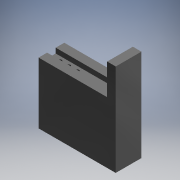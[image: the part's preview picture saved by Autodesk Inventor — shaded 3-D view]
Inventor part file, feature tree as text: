
AUTODESK INVENTOR PART (.ipt)
format: ipt  version: 2019 (Build 230136000, 136)  size: 130,560 bytes
history: native  units: mm (DEFAULTED — no unit token found)
features: sketch x4, extrude x2, hole x2
ambient origin geometry x8: Origin, YZ Plane, XZ Plane, XY Plane, X Axis, Y Axis, Z Axis, Center Point
bodies: Solid1 (feature_tree)
feature tree (8):
  extrude  "Extrusion1"  Depth=68.2498mm
  extrude  "Extrusion2"  Depth=22.86mm
  sketch  "Sketch3"  dims[d4=19.05mm d5=0.0mm d6=47.625mm]
  hole  "Hole1"  [1 undecoded]
  hole  "Hole2"  [1 undecoded]
  sketch  "Sketch1"  dims[d0=57.15mm d1=68.2498mm]
  sketch  "Sketch2"  dims[d2=50.8mm d3=22.86mm]
  sketch  "Sketch4"  dims[d7=6.35mm d8=6.35mm d9=3.7084mm d10=0.0mm d11=6.35mm d12=3.175mm d13=3.175mm d14=3.175mm d15=6.35mm d16=12.7mm d17=19.05mm d18=19.05mm d19=9.525mm d20=9.525mm d21=6.35mm d22=6.35mm d23=2.6416mm d24=7.112mm d25=9.525mm d26=6.35mm d27=14.3117mm d28=7.112mm d29=20.594885mm d30=2.6416mm d31=7.112mm d32=9.525mm d33=6.35mm d34=14.3117mm d35=7.112mm d36=20.594885mm]
note: 2 required parameter values undecoded (feature->parameter linkage not recoverable at this tier; creation-order binding heuristic only, values carry confidence <= 0.55)
